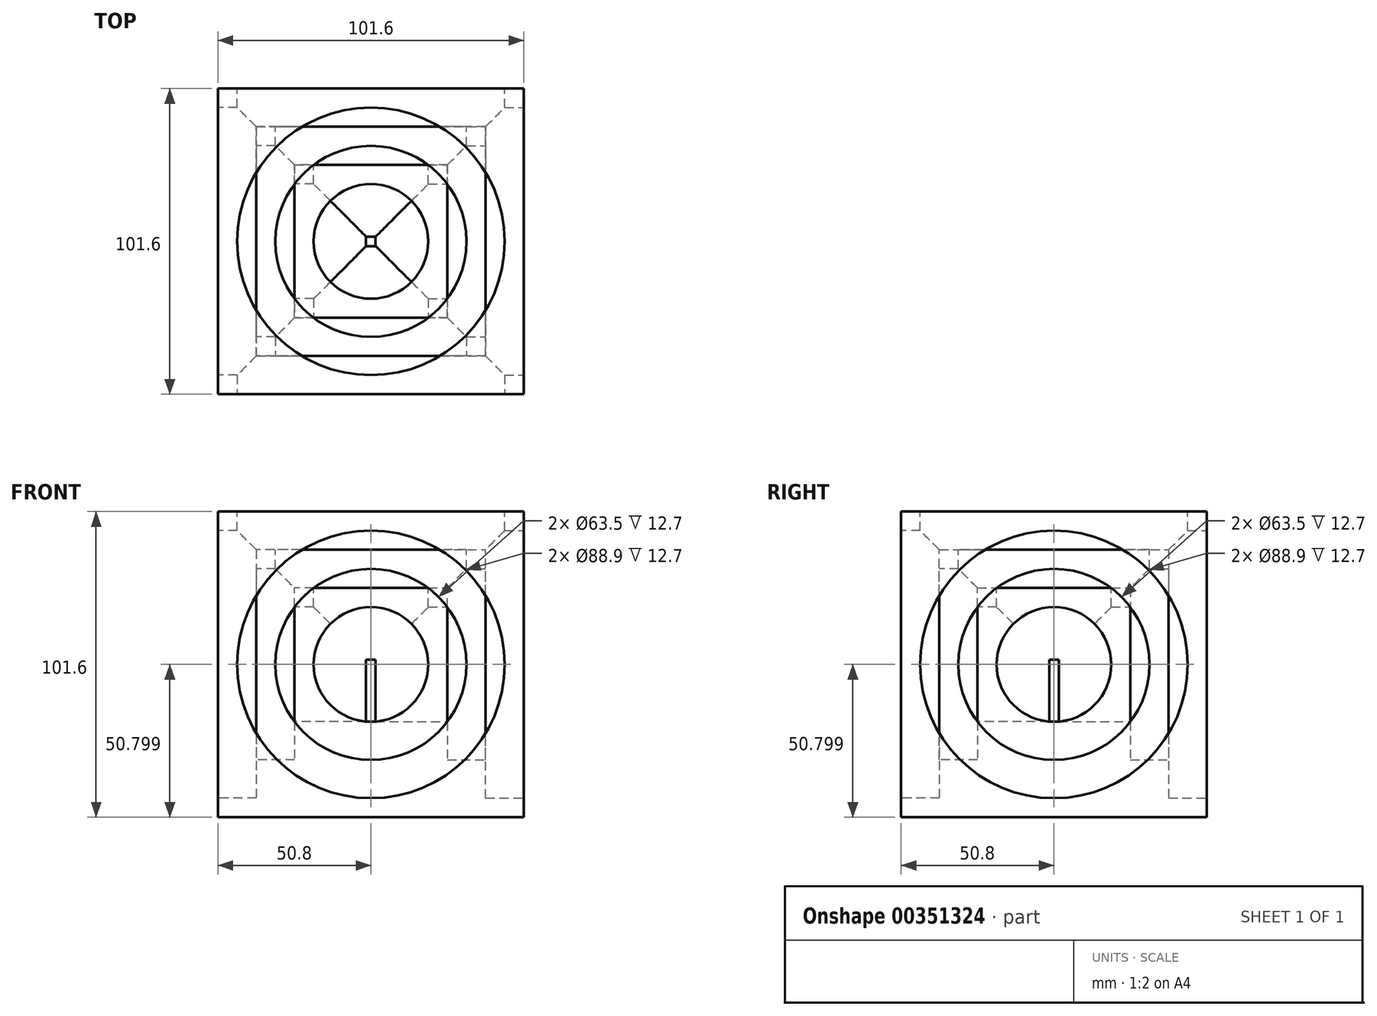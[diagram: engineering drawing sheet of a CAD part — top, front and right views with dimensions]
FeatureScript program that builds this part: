
annotation { "Feature Type Name" : "Feature", "Feature Type Description" : "" }
export const myFeature = defineFeature(function(context is Context, id is Id, definition is map)
    precondition{}
    {
        {
            var Q0;
            Q0=qCreatedBy(makeId("Front.planeOp"),FACE);
            var sketch = newSketch(context, id + "F0", { "sketchPlane" : qUnion([Q0])});
            skLineSegment(sketch, "E0.bottom", {"start": v(-101.65, 101.48) * mm, "end": v(-0.05, 101.48) * mm});
            skLineSegment(sketch, "E0.top", {"start": v(-101.65, -0.12) * mm, "end": v(-0.05, -0.12) * mm});
            skLineSegment(sketch, "E0.left", {"start": v(-101.65, 101.48) * mm, "end": v(-101.65, -0.12) * mm});
            skLineSegment(sketch, "E0.right", {"start": v(-0.05, 101.48) * mm, "end": v(-0.05, -0.12) * mm});
            skSolve(sketch);
        }
        {
            var Q0;
            Q0=makeQuery(id+"F0.imprint","IMPRINT",FACE,{"disambiguationData":[TD([[makeQuery(id+"F0.imprint","IMPRINT",EDGE,{"derivedFrom":sQuery(id+"F0.wireOp",EDGE,"E0.bottom")}),-1.0]])]});
            extrude(context, id + "F1", {"entities" : qUnion([Q0]), "depth" : 101.6 * mm});
        }
        {
            var Q0;
            Q0=makeQuery(id+"F1.opExtrude","CAP_FACE",FACE,{"disambiguationData":[OSD([sQuery(id+"F0.wireOp",EDGE,"E0.bottom"),sQuery(id+"F0.wireOp",EDGE,"E0.top"),sQuery(id+"F0.wireOp",EDGE,"E0.left"),sQuery(id+"F0.wireOp",EDGE,"E0.right")])],"isStart":false});
            var sketch = newSketch(context, id + "F2", { "sketchPlane" : qUnion([Q0])});
            skCircle(sketch, "E1", {"center": v(-50.85, 50.68) * mm, "radius": 44.45 * mm});
            skSolve(sketch);
        }
        {
            var Q0;
            Q0=makeQuery(id+"F2.imprint","IMPRINT",FACE,{"disambiguationData":[TD([[makeQuery(id+"F2.imprint","IMPRINT",EDGE,{"derivedFrom":sQuery(id+"F2.wireOp",EDGE,"E1")}),1.0]])]});
            extrude(context, id + "F3", {"entities" : qUnion([Q0]), "operationType" : NewBodyOperationType.REMOVE, "oppositeDirection" : true, "depth" : 12.7 * mm});
        }
        {
            var Q0;
            Q0=makeQuery(id+"F3.boolean.opBoolean","COPY",FACE,{"derivedFrom":makeQuery(id+"F3.opExtrude","CAP_FACE",FACE,{"disambiguationData":[OSD([sQuery(id+"F2.wireOp",EDGE,"E1")])],"isStart":false})});
            var sketch = newSketch(context, id + "F4", { "sketchPlane" : qUnion([Q0])});
            skCircle(sketch, "E2", {"center": v(-50.85, 50.68) * mm, "radius": 31.75 * mm});
            skSolve(sketch);
        }
        {
            var Q0;
            Q0=makeQuery(id+"F4.imprint","IMPRINT",FACE,{"disambiguationData":[TD([[makeQuery(id+"F4.imprint","IMPRINT",EDGE,{"derivedFrom":sQuery(id+"F4.wireOp",EDGE,"E2")}),1.0]])]});
            extrude(context, id + "F5", {"entities" : qUnion([Q0]), "operationType" : NewBodyOperationType.REMOVE, "oppositeDirection" : true, "depth" : 12.7 * mm});
        }
        {
            var Q0;
            Q0=makeQuery(id+"F5.boolean.opBoolean","COPY",FACE,{"derivedFrom":makeQuery(id+"F5.opExtrude","CAP_FACE",FACE,{"disambiguationData":[OSD([sQuery(id+"F4.wireOp",EDGE,"E2")])],"isStart":false})});
            var sketch = newSketch(context, id + "F6", { "sketchPlane" : qUnion([Q0])});
            skCircle(sketch, "E3", {"center": v(-50.85, 50.68) * mm, "radius": 19.05 * mm});
            skSolve(sketch);
        }
        {
            var Q0;
            Q0=makeQuery(id+"F6.imprint","IMPRINT",FACE,{"disambiguationData":[TD([[makeQuery(id+"F6.imprint","IMPRINT",EDGE,{"derivedFrom":sQuery(id+"F6.wireOp",EDGE,"E3")}),1.0]])]});
            extrude(context, id + "F7", {"entities" : qUnion([Q0]), "operationType" : NewBodyOperationType.REMOVE, "oppositeDirection" : true, "depth" : 23.8 * mm});
        }
        {
            var Q0;
            Q0=makeQuery(id+"F1.opExtrude","SWEPT_FACE",FACE,{"disambiguationData":[OSD([sQuery(id+"F0.wireOp",EDGE,"E0.bottom")])]});
            var sketch = newSketch(context, id + "F8", { "sketchPlane" : qUnion([Q0])});
            skCircle(sketch, "E4", {"center": v(-50.85, -50.8) * mm, "radius": 44.45 * mm});
            skCircle(sketch, "E5", {"center": v(-50.85, -50.8) * mm, "radius": 31.75 * mm});
            skCircle(sketch, "E6", {"center": v(-50.85, -50.8) * mm, "radius": 19.05 * mm});
            skSolve(sketch);
        }
        {
            var Q0;
            Q0 = qSketchRegion(id + "F8", true);
            var Q1;
            Q1=makeQuery(id+"F8.imprint","IMPRINT",FACE,{"disambiguationData":[TD([[makeQuery(id+"F8.imprint","IMPRINT",EDGE,{"derivedFrom":sQuery(id+"F8.wireOp",EDGE,"E5")}),1.0]])]});
            var Q2;
            Q2=makeQuery(id+"F8.imprint","IMPRINT",FACE,{"disambiguationData":[TD([[makeQuery(id+"F8.imprint","IMPRINT",EDGE,{"derivedFrom":sQuery(id+"F8.wireOp",EDGE,"E6")}),1.0]])]});
            extrude(context, id + "F9", {"entities" : qUnion([Q0, Q1, Q2]), "operationType" : NewBodyOperationType.REMOVE, "oppositeDirection" : true, "depth" : 12.7 * mm});
        }
        {
            var Q0;
            Q0=makeQuery(id+"F8.imprint","IMPRINT",FACE,{"disambiguationData":[TD([[makeQuery(id+"F8.imprint","IMPRINT",EDGE,{"derivedFrom":sQuery(id+"F8.wireOp",EDGE,"E5")}),1.0]])]});
            var Q1;
            Q1=makeQuery(id+"F8.imprint","IMPRINT",FACE,{"disambiguationData":[TD([[makeQuery(id+"F8.imprint","IMPRINT",EDGE,{"derivedFrom":sQuery(id+"F8.wireOp",EDGE,"E6")}),1.0]])]});
            extrude(context, id + "F10", {"entities" : qUnion([Q0, Q1]), "operationType" : NewBodyOperationType.REMOVE, "oppositeDirection" : true, "depth" : 25.4 * mm});
        }
        {
            var Q0;
            Q0=makeQuery(id+"F8.imprint","IMPRINT",FACE,{"disambiguationData":[TD([[makeQuery(id+"F8.imprint","IMPRINT",EDGE,{"derivedFrom":sQuery(id+"F8.wireOp",EDGE,"E6")}),1.0]])]});
            extrude(context, id + "F11", {"entities" : qUnion([Q0]), "operationType" : NewBodyOperationType.REMOVE, "oppositeDirection" : true, "depth" : 49.23 * mm});
        }
        {
            var Q0;
            Q0=makeQuery(id+"F1.opExtrude","SWEPT_FACE",FACE,{"disambiguationData":[OSD([sQuery(id+"F0.wireOp",EDGE,"E0.right")])]});
            var sketch = newSketch(context, id + "F12", { "sketchPlane" : qUnion([Q0])});
            skCircle(sketch, "E7", {"center": v(-50.8, 50.68) * mm, "radius": 44.45 * mm});
            skCircle(sketch, "E8", {"center": v(-50.8, 50.68) * mm, "radius": 31.75 * mm});
            skCircle(sketch, "E9", {"center": v(-50.8, 50.68) * mm, "radius": 19.05 * mm});
            skSolve(sketch);
        }
        {
            var Q0;
            Q0=makeQuery(id+"F1.opExtrude","CAP_FACE",FACE,{"disambiguationData":[OSD([sQuery(id+"F0.wireOp",EDGE,"E0.bottom"),sQuery(id+"F0.wireOp",EDGE,"E0.top"),sQuery(id+"F0.wireOp",EDGE,"E0.left"),sQuery(id+"F0.wireOp",EDGE,"E0.right")])],"isStart":true});
            var sketch = newSketch(context, id + "F13", { "sketchPlane" : qUnion([Q0])});
            skCircle(sketch, "E10", {"center": v(50.85, 50.68) * mm, "radius": 44.45 * mm});
            skCircle(sketch, "E11", {"center": v(50.85, 50.68) * mm, "radius": 31.75 * mm});
            skCircle(sketch, "E12", {"center": v(50.85, 50.68) * mm, "radius": 19.05 * mm});
            skSolve(sketch);
        }
        {
            var Q0;
            Q0=makeQuery(id+"F1.opExtrude","SWEPT_FACE",FACE,{"disambiguationData":[OSD([sQuery(id+"F0.wireOp",EDGE,"E0.left")])]});
            var sketch = newSketch(context, id + "F14", { "sketchPlane" : qUnion([Q0])});
            skCircle(sketch, "E13", {"center": v(50.8, 50.68) * mm, "radius": 44.45 * mm});
            skCircle(sketch, "E14", {"center": v(50.8, 50.68) * mm, "radius": 31.75 * mm});
            skCircle(sketch, "E15", {"center": v(50.8, 50.68) * mm, "radius": 19.05 * mm});
            skSolve(sketch);
        }
        {
            var Q0;
            Q0=makeQuery(id+"F12.imprint","IMPRINT",FACE,{"disambiguationData":[TD([[makeQuery(id+"F12.imprint","IMPRINT",EDGE,{"derivedFrom":sQuery(id+"F12.wireOp",EDGE,"E9")}),1.0]])]});
            extrude(context, id + "F15", {"entities" : qUnion([Q0]), "operationType" : NewBodyOperationType.REMOVE, "oppositeDirection" : true, "depth" : 49.23 * mm});
        }
        {
            var Q0;
            Q0=makeQuery(id+"F13.imprint","IMPRINT",FACE,{"disambiguationData":[TD([[makeQuery(id+"F13.imprint","IMPRINT",EDGE,{"derivedFrom":sQuery(id+"F13.wireOp",EDGE,"E12")}),1.0]])]});
            extrude(context, id + "F16", {"entities" : qUnion([Q0]), "operationType" : NewBodyOperationType.REMOVE, "oppositeDirection" : true, "depth" : 49.23 * mm});
        }
        {
            var Q0;
            Q0=makeQuery(id+"F13.imprint","IMPRINT",FACE,{"disambiguationData":[TD([[makeQuery(id+"F13.imprint","IMPRINT",EDGE,{"derivedFrom":sQuery(id+"F13.wireOp",EDGE,"E11")}),1.0]])]});
            extrude(context, id + "F17", {"entities" : qUnion([Q0]), "operationType" : NewBodyOperationType.REMOVE, "oppositeDirection" : true, "depth" : 25.4 * mm});
        }
        {
            var Q0;
            Q0=makeQuery(id+"F13.imprint","IMPRINT",FACE,{"disambiguationData":[TD([[makeQuery(id+"F13.imprint","IMPRINT",EDGE,{"derivedFrom":sQuery(id+"F13.wireOp",EDGE,"E10")}),1.0]])]});
            extrude(context, id + "F18", {"entities" : qUnion([Q0]), "operationType" : NewBodyOperationType.REMOVE, "oppositeDirection" : true, "depth" : 12.7 * mm});
        }
        {
            var Q0;
            Q0=makeQuery(id+"F14.imprint","IMPRINT",FACE,{"disambiguationData":[TD([[makeQuery(id+"F14.imprint","IMPRINT",EDGE,{"derivedFrom":sQuery(id+"F14.wireOp",EDGE,"E15")}),1.0]])]});
            extrude(context, id + "F19", {"entities" : qUnion([Q0]), "operationType" : NewBodyOperationType.REMOVE, "oppositeDirection" : true, "depth" : 49.2 * mm});
        }
        {
            var Q0;
            Q0=makeQuery(id+"F14.imprint","IMPRINT",FACE,{"disambiguationData":[TD([[makeQuery(id+"F14.imprint","IMPRINT",EDGE,{"derivedFrom":sQuery(id+"F14.wireOp",EDGE,"E14")}),1.0]])]});
            extrude(context, id + "F20", {"entities" : qUnion([Q0]), "operationType" : NewBodyOperationType.REMOVE, "oppositeDirection" : true, "depth" : 25.4 * mm});
        }
        {
            var Q0;
            Q0=makeQuery(id+"F14.imprint","IMPRINT",FACE,{"disambiguationData":[TD([[makeQuery(id+"F14.imprint","IMPRINT",EDGE,{"derivedFrom":sQuery(id+"F14.wireOp",EDGE,"E13")}),1.0]])]});
            extrude(context, id + "F21", {"entities" : qUnion([Q0]), "operationType" : NewBodyOperationType.REMOVE, "oppositeDirection" : true, "depth" : 12.7 * mm});
        }
        {
            var Q0;
            Q0=makeQuery(id+"F12.imprint","IMPRINT",FACE,{"disambiguationData":[TD([[makeQuery(id+"F12.imprint","IMPRINT",EDGE,{"derivedFrom":sQuery(id+"F12.wireOp",EDGE,"E8")}),1.0]])]});
            extrude(context, id + "F22", {"entities" : qUnion([Q0]), "operationType" : NewBodyOperationType.REMOVE, "oppositeDirection" : true, "depth" : 25.4 * mm});
        }
        {
            var Q0;
            Q0=makeQuery(id+"F12.imprint","IMPRINT",FACE,{"disambiguationData":[TD([[makeQuery(id+"F12.imprint","IMPRINT",EDGE,{"derivedFrom":sQuery(id+"F12.wireOp",EDGE,"E7")}),1.0]])]});
            extrude(context, id + "F23", {"entities" : qUnion([Q0]), "operationType" : NewBodyOperationType.REMOVE, "oppositeDirection" : true, "depth" : 12.7 * mm});
        }
    });
